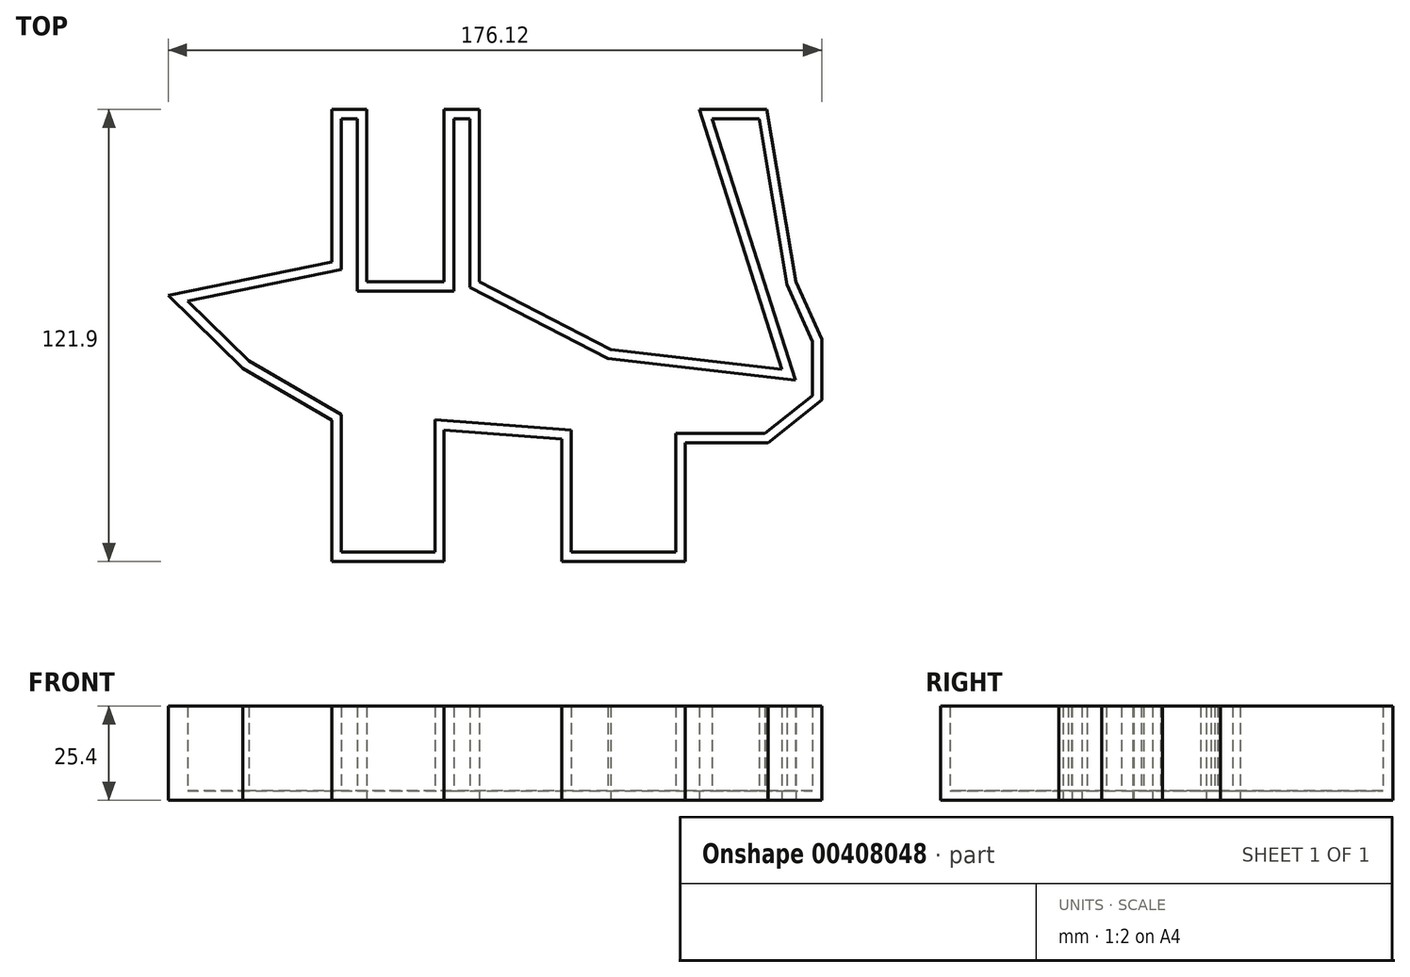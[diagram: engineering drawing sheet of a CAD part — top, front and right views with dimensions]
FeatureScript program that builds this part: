
annotation { "Feature Type Name" : "Feature", "Feature Type Description" : "" }
export const myFeature = defineFeature(function(context is Context, id is Id, definition is map)
    precondition{}
    {
        {
            var Q0;
            Q0=qCreatedBy(makeId("Top.planeOp"),FACE);
            var sketch = newSketch(context, id + "F0", { "sketchPlane" : qUnion([Q0])});
            skLineSegment(sketch, "E0", {"start": v(-49.4, 46.45) * mm, "end": v(-49.4, 0) * mm});
            skLineSegment(sketch, "E1", {"start": v(-49.4, 46.45) * mm, "end": v(-40, 46.45) * mm});
            skLineSegment(sketch, "E2", {"start": v(-40, 46.45) * mm, "end": v(-40, 0) * mm});
            skLineSegment(sketch, "E3", {"start": v(-40, 0) * mm, "end": v(-19.06, 0) * mm});
            skLineSegment(sketch, "E4", {"start": v(-19.06, 0) * mm, "end": v(-19.06, 46.45) * mm});
            skLineSegment(sketch, "E5", {"start": v(-19.06, 46.45) * mm, "end": v(-9.67, 46.45) * mm});
            skLineSegment(sketch, "E6", {"start": v(-9.67, 46.45) * mm, "end": v(-9.67, 0) * mm});
            skLineSegment(sketch, "E7", {"start": v(-9.67, 0) * mm, "end": v(25.78, -18.26) * mm});
            skLineSegment(sketch, "E8", {"start": v(25.78, -18.26) * mm, "end": v(71.96, -23.63) * mm});
            skLineSegment(sketch, "E9", {"start": v(71.96, -23.63) * mm, "end": v(49.67, 46.45) * mm});
            skLineSegment(sketch, "E10", {"start": v(49.67, 46.45) * mm, "end": v(67.93, 46.45) * mm});
            skLineSegment(sketch, "E11", {"start": v(67.93, 46.45) * mm, "end": v(75.71, 0) * mm});
            skLineSegment(sketch, "E12", {"start": v(75.71, 0) * mm, "end": v(82.7, -15.58) * mm});
            skLineSegment(sketch, "E13", {"start": v(82.7, -15.58) * mm, "end": v(82.7, -31.95) * mm});
            skLineSegment(sketch, "E14", {"start": v(82.7, -31.95) * mm, "end": v(68.2, -43.5) * mm});
            skLineSegment(sketch, "E15", {"start": v(68.2, -43.5) * mm, "end": v(45.91, -43.5) * mm});
            skLineSegment(sketch, "E16", {"start": v(45.91, -43.5) * mm, "end": v(45.91, -75.45) * mm});
            skLineSegment(sketch, "E17", {"start": v(45.91, -75.45) * mm, "end": v(12.62, -75.45) * mm});
            skLineSegment(sketch, "E18", {"start": v(12.62, -75.45) * mm, "end": v(12.62, -42.42) * mm});
            skLineSegment(sketch, "E19", {"start": v(12.62, -42.42) * mm, "end": v(-19.06, -40) * mm});
            skLineSegment(sketch, "E20", {"start": v(-19.06, -40) * mm, "end": v(-19.06, -75.45) * mm});
            skLineSegment(sketch, "E21", {"start": v(-19.06, -75.45) * mm, "end": v(-49.4, -75.45) * mm});
            skLineSegment(sketch, "E22", {"start": v(-49.4, -75.45) * mm, "end": v(-49.4, -37.32) * mm});
            skLineSegment(sketch, "E23", {"start": v(-49.4, -37.32) * mm, "end": v(-73.3, -23.36) * mm});
            skLineSegment(sketch, "E24", {"start": v(-73.3, -23.36) * mm, "end": v(-93.43, -3.76) * mm});
            skLineSegment(sketch, "E25", {"start": v(-93.43, -3.76) * mm, "end": v(-49.4, 5.37) * mm});
            skSolve(sketch);
        }
        {
            var Q0;
            {var subQ0=sQuery(id+"F0.wireOp",EDGE,"E1");Q0=makeQuery(id+"F0.imprint","IMPRINT",FACE,{"disambiguationData":[TD([[makeQuery(id+"F0.imprint","IMPRINT",EDGE,{"derivedFrom":subQ0}),-1.0]])]});}
            extrude(context, id + "F1", {"entities" : qUnion([Q0]), "depth" : 25.4 * mm});
        }
        {
            var Q0;
            Q0=makeQuery(id+"F1.opExtrude","CAP_FACE",FACE,{"disambiguationData":[OSD([sQuery(id+"F0.wireOp",EDGE,"E0"),sQuery(id+"F0.wireOp",EDGE,"E1"),sQuery(id+"F0.wireOp",EDGE,"E2"),sQuery(id+"F0.wireOp",EDGE,"E3"),sQuery(id+"F0.wireOp",EDGE,"E4"),sQuery(id+"F0.wireOp",EDGE,"E5"),sQuery(id+"F0.wireOp",EDGE,"E6"),sQuery(id+"F0.wireOp",EDGE,"E7"),sQuery(id+"F0.wireOp",EDGE,"E8"),sQuery(id+"F0.wireOp",EDGE,"E9"),sQuery(id+"F0.wireOp",EDGE,"E10"),sQuery(id+"F0.wireOp",EDGE,"E11"),sQuery(id+"F0.wireOp",EDGE,"E12"),sQuery(id+"F0.wireOp",EDGE,"E13"),sQuery(id+"F0.wireOp",EDGE,"E14"),sQuery(id+"F0.wireOp",EDGE,"E15"),sQuery(id+"F0.wireOp",EDGE,"E16"),sQuery(id+"F0.wireOp",EDGE,"E17"),sQuery(id+"F0.wireOp",EDGE,"E18"),sQuery(id+"F0.wireOp",EDGE,"E19"),sQuery(id+"F0.wireOp",EDGE,"E20"),sQuery(id+"F0.wireOp",EDGE,"E21"),sQuery(id+"F0.wireOp",EDGE,"E22"),sQuery(id+"F0.wireOp",EDGE,"E23"),sQuery(id+"F0.wireOp",EDGE,"E24"),sQuery(id+"F0.wireOp",EDGE,"E25")])],"isStart":false});
            shell(context, id + "F2", {"entities" : qUnion([Q0]), "thickness" : 2.54 * mm});
        }
    });
